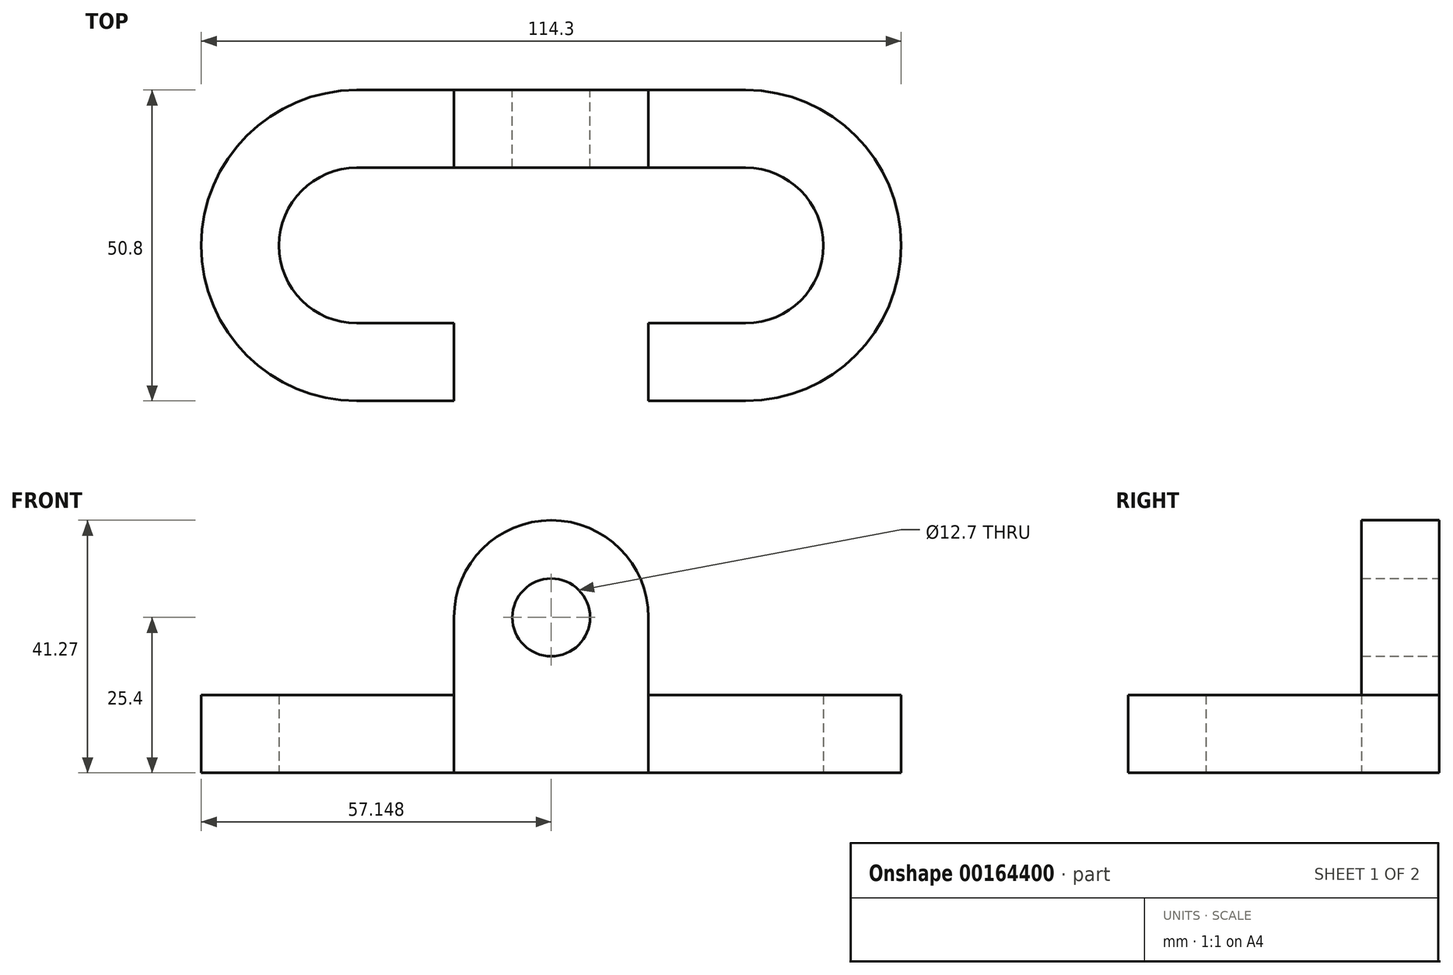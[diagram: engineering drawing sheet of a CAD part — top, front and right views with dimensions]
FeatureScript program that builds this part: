
annotation { "Feature Type Name" : "Feature", "Feature Type Description" : "" }
export const myFeature = defineFeature(function(context is Context, id is Id, definition is map)
    precondition{}
    {
        {
            var Q0;
            Q0=qCreatedBy(makeId("Top.planeOp"),FACE);
            var sketch = newSketch(context, id + "F0", { "sketchPlane" : qUnion([Q0])});
            skLineSegment(sketch, "E0", {"start": v(27.67, 2.76) * mm, "end": v(27.67, -9.94) * mm});
            skLineSegment(sketch, "E1", {"start": v(27.67, -9.94) * mm, "end": v(43.55, -9.94) * mm});
            skLineSegment(sketch, "E2", {"start": v(27.67, 2.76) * mm, "end": v(43.55, 2.76) * mm});
            skLineSegment(sketch, "E3", {"start": v(-4.08, 2.76) * mm, "end": v(-4.08, -9.94) * mm});
            skLineSegment(sketch, "E4", {"start": v(-4.08, -9.94) * mm, "end": v(-19.95, -9.94) * mm});
            skLineSegment(sketch, "E5", {"start": v(-4.08, 2.76) * mm, "end": v(-19.95, 2.76) * mm});
            skLineSegment(sketch, "E6", {"start": v(-19.95, 28.16) * mm, "end": v(43.55, 28.16) * mm});
            skLineSegment(sketch, "E7", {"start": v(43.55, 40.86) * mm, "end": v(-19.95, 40.86) * mm});
            skArc(sketch, "E8", {"start": v(43.55, -9.94) * mm, "mid": v(68.95, 15.46) * mm, "end": v(43.55, 40.86) * mm});
            skArc(sketch, "E9", {"start": v(43.55, 2.76) * mm, "mid": v(56.25, 15.46) * mm, "end": v(43.55, 28.16) * mm});
            skArc(sketch, "E10", {"start": v(-19.95, 40.86) * mm, "mid": v(-45.35, 15.46) * mm, "end": v(-19.95, -9.94) * mm});
            skArc(sketch, "E11", {"start": v(-19.95, 2.76) * mm, "mid": v(-32.65, 15.46) * mm, "end": v(-19.95, 28.16) * mm});
            skSolve(sketch);
        }
        {
            var Q0;
            Q0=makeQuery(id+"F0.imprint","IMPRINT",FACE,{"disambiguationData":[TD([[makeQuery(id+"F0.imprint","IMPRINT",EDGE,{"derivedFrom":sQuery(id+"F0.wireOp",EDGE,"E0")}),1.0]])]});
            extrude(context, id + "F1", {"entities" : qUnion([Q0]), "depth" : 12.7 * mm});
        }
        {
            var Q0;
            Q0=makeQuery(id+"F1.opExtrude","SWEPT_FACE",FACE,{"disambiguationData":[OSD([sQuery(id+"F0.wireOp",EDGE,"E7")])]});
            var sketch = newSketch(context, id + "F2", { "sketchPlane" : qUnion([Q0])});
            skLineSegment(sketch, "E12", {"start": v(-34.27, 25.4) * mm, "end": v(12.7, 25.4) * mm, "construction": true});
            skLineSegment(sketch, "E13", {"start": v(-27.67, 12.7) * mm, "end": v(4.08, 12.7) * mm});
            skLineSegment(sketch, "E14", {"start": v(-27.67, 12.7) * mm, "end": v(-27.67, 25.4) * mm});
            skLineSegment(sketch, "E15", {"start": v(-27.67, 25.4) * mm, "end": v(4.08, 25.4) * mm});
            skLineSegment(sketch, "E16", {"start": v(4.08, 25.4) * mm, "end": v(4.08, 12.7) * mm});
            skPoint(sketch, "E17", {"position": v(-11.8, 25.4) * mm});
            skArc(sketch, "E18", {"start": v(4.08, 25.4) * mm, "mid": v(-11.8, 41.28) * mm, "end": v(-27.67, 25.4) * mm});
            skSolve(sketch);
        }
        {
            var Q0;
            Q0=makeQuery(id+"F2.imprint","IMPRINT",FACE,{"disambiguationData":[TD([[makeQuery(id+"F2.imprint","IMPRINT",EDGE,{"derivedFrom":sQuery(id+"F2.wireOp",EDGE,"E13")}),1.0]])]});
            var Q1;
            Q1=makeQuery(id+"F2.imprint","IMPRINT",FACE,{"disambiguationData":[TD([[makeQuery(id+"F2.imprint","IMPRINT",EDGE,{"derivedFrom":sQuery(id+"F2.wireOp",EDGE,"E15")}),1.0]])]});
            extrude(context, id + "F3", {"entities" : qUnion([Q0, Q1]), "operationType" : NewBodyOperationType.ADD, "oppositeDirection" : true, "depth" : 12.7 * mm});
        }
        {
            var Q0;
            Q0=sQuery(id+"F2.wireOp",VERTEX,"E17");
            var Q1;
            Q1=makeQuery(id+"F1.opExtrude","SWEPT_BODY",BODY,{"disambiguationData":[OSD([sQuery(id+"F0.wireOp",EDGE,"E0"),sQuery(id+"F0.wireOp",EDGE,"E1"),sQuery(id+"F0.wireOp",EDGE,"E2"),sQuery(id+"F0.wireOp",EDGE,"E3"),sQuery(id+"F0.wireOp",EDGE,"E4"),sQuery(id+"F0.wireOp",EDGE,"E5"),sQuery(id+"F0.wireOp",EDGE,"E6"),sQuery(id+"F0.wireOp",EDGE,"E7"),sQuery(id+"F0.wireOp",EDGE,"E8"),sQuery(id+"F0.wireOp",EDGE,"E9"),sQuery(id+"F0.wireOp",EDGE,"E10"),sQuery(id+"F0.wireOp",EDGE,"E11")])]});
            hole(context, id + "F4", {"style" : HoleStyle.SIMPLE, "endStyle" : HoleEndStyle.THROUGH, "holeDiameter" : 12.7 * mm, "locations" : qUnion([Q0]), "scope" : qUnion([Q1]), "isTappedThrough" : true});
        }
    });
